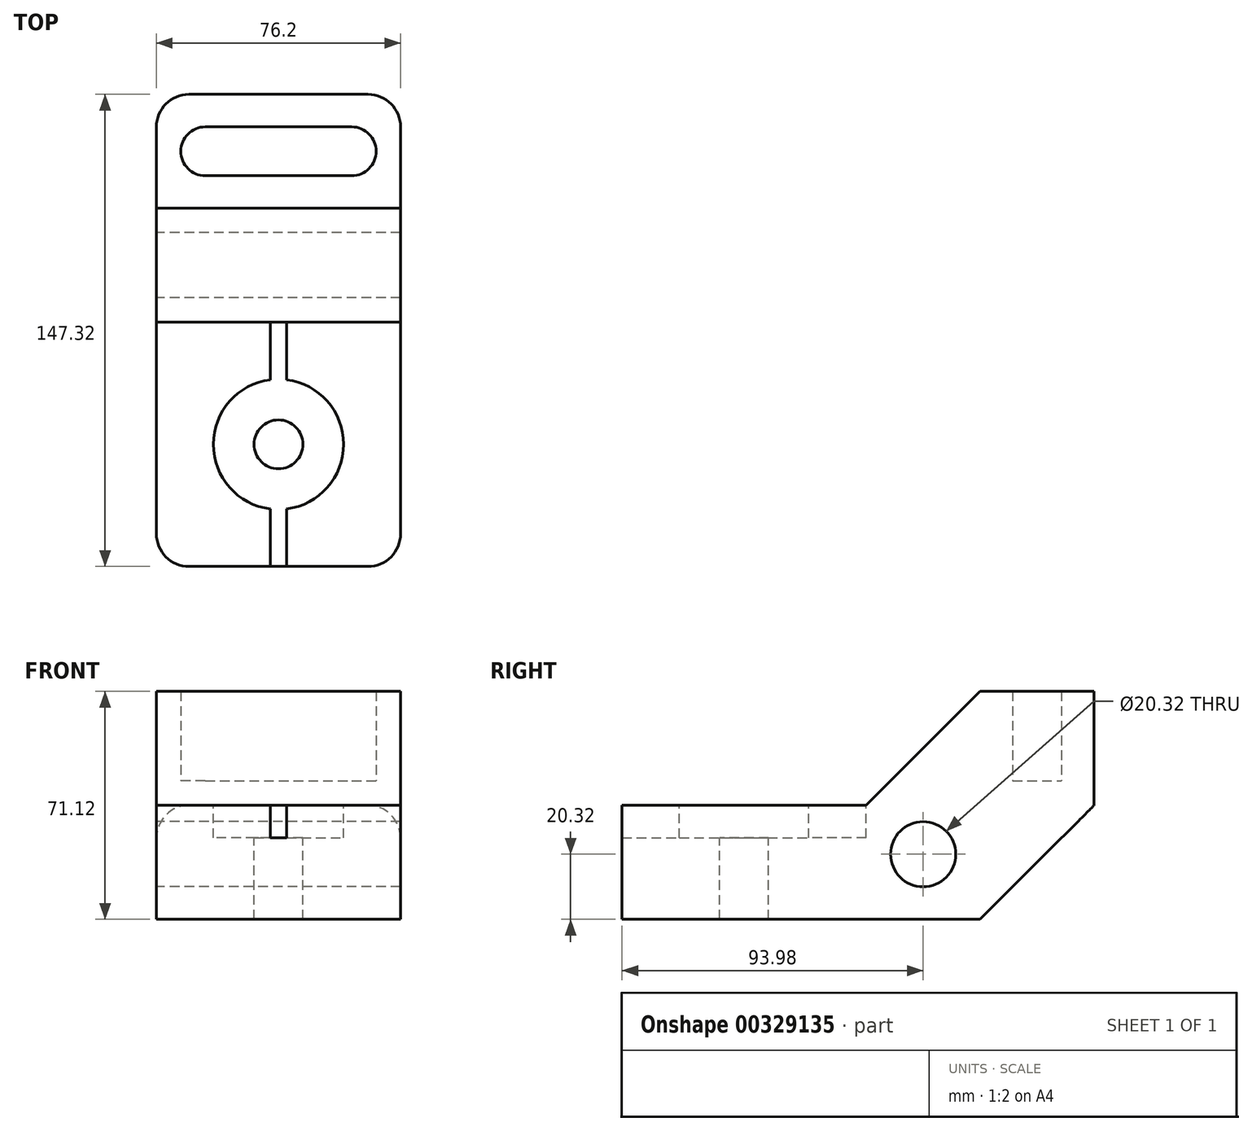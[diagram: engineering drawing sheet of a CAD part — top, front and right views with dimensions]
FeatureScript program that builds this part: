
annotation { "Feature Type Name" : "Feature", "Feature Type Description" : "" }
export const myFeature = defineFeature(function(context is Context, id is Id, definition is map)
    precondition{}
    {
        {
            var Q0;
            Q0=qCreatedBy(makeId("Right.planeOp"),FACE);
            var sketch = newSketch(context, id + "F0", { "sketchPlane" : qUnion([Q0])});
            skCircle(sketch, "E0", {"center": v(0, 0) * mm, "radius": 10.16 * mm});
            skLineSegment(sketch, "E1", {"start": v(-93.98, 15.24) * mm, "end": v(-93.98, -20.32) * mm});
            skLineSegment(sketch, "E2", {"start": v(-93.98, -20.32) * mm, "end": v(17.78, -20.32) * mm});
            skLineSegment(sketch, "E3", {"start": v(17.78, -20.32) * mm, "end": v(53.34, 15.24) * mm});
            skLineSegment(sketch, "E4", {"start": v(53.34, 15.24) * mm, "end": v(53.34, 50.8) * mm});
            skLineSegment(sketch, "E5", {"start": v(53.34, 50.8) * mm, "end": v(17.78, 50.8) * mm});
            skLineSegment(sketch, "E6", {"start": v(17.78, 50.8) * mm, "end": v(-17.78, 15.24) * mm});
            skLineSegment(sketch, "E7", {"start": v(-17.78, 15.24) * mm, "end": v(-93.98, 15.24) * mm});
            skSolve(sketch);
        }
        {
            var Q0;
            Q0=makeQuery(id+"F0.imprint","IMPRINT",FACE,{"disambiguationData":[TD([[makeQuery(id+"F0.imprint","IMPRINT",EDGE,{"derivedFrom":sQuery(id+"F0.wireOp",EDGE,"E0")}),-1.0]])]});
            extrude(context, id + "F1", {"entities" : qUnion([Q0]), "depth" : 76.2 * mm, "symmetric" : true});
        }
        {
            var Q0;
            Q0=makeQuery(id+"F1.opExtrude","SWEPT_FACE",FACE,{"disambiguationData":[OSD([sQuery(id+"F0.wireOp",EDGE,"E7")])]});
            var sketch = newSketch(context, id + "F2", { "sketchPlane" : qUnion([Q0])});
            skPoint(sketch, "E8", {"position": v(0, -17.78) * mm});
            skPoint(sketch, "E9", {"position": v(0, -93.98) * mm});
            skPoint(sketch, "E10", {"position": v(0, -55.88) * mm});
            skLineSegment(sketch, "E11", {"start": v(2.54, -17.78) * mm, "end": v(2.54, -93.98) * mm});
            skLineSegment(sketch, "E12", {"start": v(-2.54, -93.98) * mm, "end": v(2.54, -93.98) * mm});
            skLineSegment(sketch, "E13", {"start": v(-2.54, -93.98) * mm, "end": v(-2.54, -17.78) * mm});
            skLineSegment(sketch, "E14", {"start": v(2.54, -17.78) * mm, "end": v(-2.54, -17.78) * mm});
            skLineSegment(sketch, "E15", {"start": v(-22.86, 43.18) * mm, "end": v(22.86, 43.18) * mm});
            skLineSegment(sketch, "E16", {"start": v(-22.86, 27.94) * mm, "end": v(22.86, 27.94) * mm});
            skArc(sketch, "E17", {"start": v(22.86, 43.18) * mm, "mid": v(30.48, 35.56) * mm, "end": v(22.86, 27.94) * mm});
            skArc(sketch, "E18", {"start": v(-22.86, 27.94) * mm, "mid": v(-30.48, 35.56) * mm, "end": v(-22.86, 43.18) * mm});
            skSolve(sketch);
        }
        {
            var Q0;
            Q0=makeQuery(id+"F2.imprint","IMPRINT",FACE,{"disambiguationData":[TD([[makeQuery(id+"F2.imprint","IMPRINT",EDGE,{"derivedFrom":sQuery(id+"F2.wireOp",EDGE,"E15")}),-1.0]])]});
            extrude(context, id + "F3", {"entities" : qUnion([Q0]), "operationType" : NewBodyOperationType.REMOVE, "endBound" : BoundingType.THROUGH_ALL, "depth" : 115.32 * mm, "hasSecondDirection" : true, "secondDirectionOppositeDirection" : false, "secondDirectionDepth" : 7.62 * mm});
        }
        {
            var Q0;
            Q0=sQuery(id+"F2.wireOp",VERTEX,"E10");
            var Q1;
            Q1=makeQuery(id+"F1.opExtrude","SWEPT_BODY",BODY,{"disambiguationData":[OSD([sQuery(id+"F0.wireOp",EDGE,"E0"),sQuery(id+"F0.wireOp",EDGE,"E1"),sQuery(id+"F0.wireOp",EDGE,"E2"),sQuery(id+"F0.wireOp",EDGE,"E3"),sQuery(id+"F0.wireOp",EDGE,"E4"),sQuery(id+"F0.wireOp",EDGE,"E5"),sQuery(id+"F0.wireOp",EDGE,"E6"),sQuery(id+"F0.wireOp",EDGE,"E7")])]});
            hole(context, id + "F4", {"style" : HoleStyle.C_BORE, "endStyle" : HoleEndStyle.THROUGH, "holeDiameter" : 15.24 * mm, "cBoreDiameter" : 40.64 * mm, "cBoreDepth" : 10.16 * mm, "tappedDepth" : 12.7 * mm, "tapClearance" : 3, "locations" : qUnion([Q0]), "scope" : qUnion([Q1])});
        }
        {
            var Q0;
            Q0=makeQuery(id+"F2.imprint","IMPRINT",FACE,{"disambiguationData":[TD([[makeQuery(id+"F2.imprint","IMPRINT",EDGE,{"derivedFrom":sQuery(id+"F2.wireOp",EDGE,"E11")}),-1.0]])]});
            extrude(context, id + "F5", {"entities" : qUnion([Q0]), "operationType" : NewBodyOperationType.REMOVE, "oppositeDirection" : true, "depth" : 10.16 * mm});
        }
        {
            var Q0;
            Q0=makeQuery(id+"F1.opExtrude","CAP_EDGE",EDGE,{"disambiguationData":[OSD([sQuery(id+"F0.wireOp",EDGE,"E1")])],"isStart":false});
            var Q1;
            Q1=makeQuery(id+"F1.opExtrude","CAP_EDGE",EDGE,{"disambiguationData":[OSD([sQuery(id+"F0.wireOp",EDGE,"E1")])],"isStart":true});
            var Q2;
            Q2=makeQuery(id+"F1.opExtrude","CAP_EDGE",EDGE,{"disambiguationData":[OSD([sQuery(id+"F0.wireOp",EDGE,"E4")])],"isStart":false});
            var Q3;
            Q3=makeQuery(id+"F1.opExtrude","CAP_EDGE",EDGE,{"disambiguationData":[OSD([sQuery(id+"F0.wireOp",EDGE,"E4")])],"isStart":true});
            fillet(context, id + "F6", {"entities" : qUnion([Q0, Q1, Q2, Q3]), "radius" : 10.16 * mm, "tangentPropagation" : true, "allowEdgeOverflow" : false});
        }
    });
